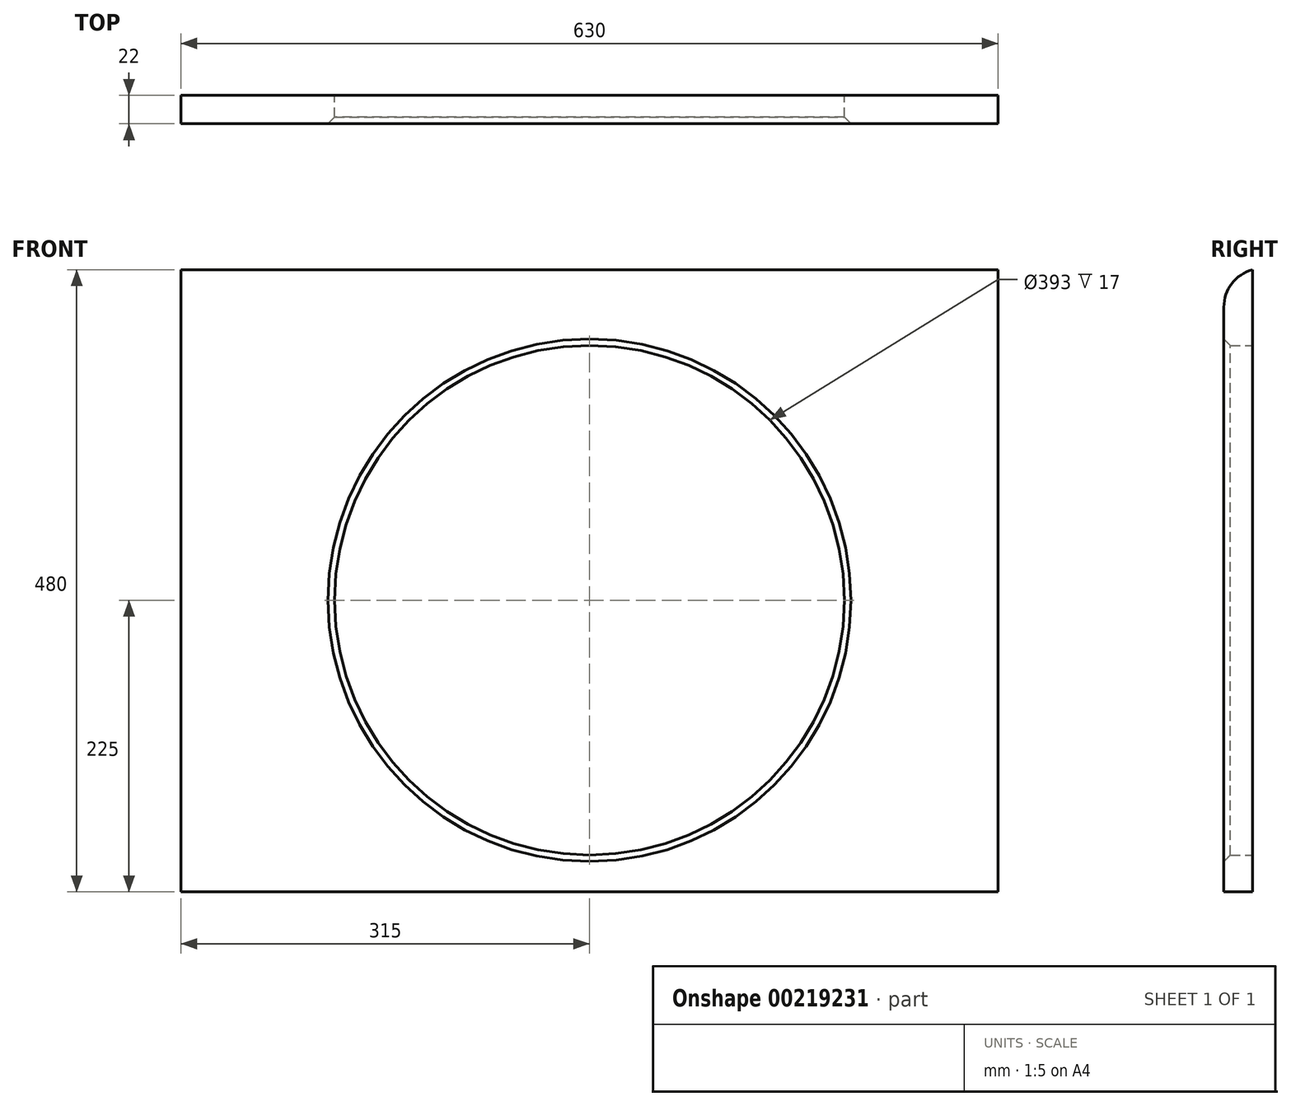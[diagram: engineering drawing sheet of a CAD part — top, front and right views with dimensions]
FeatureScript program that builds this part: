
annotation { "Feature Type Name" : "Feature", "Feature Type Description" : "" }
export const myFeature = defineFeature(function(context is Context, id is Id, definition is map)
    precondition{}
    {
        {
            var Q0;
            Q0=qCreatedBy(makeId("Front.planeOp"),FACE);
            var sketch = newSketch(context, id + "F0", { "sketchPlane" : qUnion([Q0])});
            skLineSegment(sketch, "E0.bottom", {"start": v(315, 240) * mm, "end": v(-315, 240) * mm});
            skLineSegment(sketch, "E0.top", {"start": v(315, -240) * mm, "end": v(-315, -240) * mm});
            skLineSegment(sketch, "E0.left", {"start": v(315, 240) * mm, "end": v(315, -240) * mm});
            skLineSegment(sketch, "E0.right", {"start": v(-315, 240) * mm, "end": v(-315, -240) * mm});
            skPoint(sketch, "E0.middle", {"position": v(0, 0) * mm});
            skCircle(sketch, "E1", {"center": v(0, -15) * mm, "radius": 196.5 * mm});
            skSolve(sketch);
        }
        {
            var Q0;
            Q0=makeQuery(id+"F0.imprint","IMPRINT",FACE,{"disambiguationData":[TD([[makeQuery(id+"F0.imprint","IMPRINT",EDGE,{"derivedFrom":sQuery(id+"F0.wireOp",EDGE,"E0.bottom")}),1.0]])]});
            extrude(context, id + "F1", {"entities" : qUnion([Q0]), "depth" : 22 * mm});
        }
        {
            var Q0;
            Q0=makeQuery(id+"F1.opExtrude","CAP_EDGE",EDGE,{"disambiguationData":[OSD([sQuery(id+"F0.wireOp",EDGE,"E0.bottom")])],"isStart":false});
            fillet(context, id + "F2", {"entities" : qUnion([Q0]), "radius" : 30 * mm, "tangentPropagation" : true, "allowEdgeOverflow" : false});
        }
        {
            var Q0;
            Q0=makeQuery(id+"F1.opExtrude","CAP_EDGE",EDGE,{"disambiguationData":[OSD([sQuery(id+"F0.wireOp",EDGE,"E1")])],"isStart":false});
            chamfer(context, id + "F3", {"entities" : qUnion([Q0]), "width" : 5 * mm, "tangentPropagation" : true});
        }
    });
